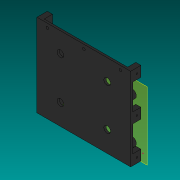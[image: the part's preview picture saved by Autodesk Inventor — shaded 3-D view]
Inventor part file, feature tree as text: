
AUTODESK INVENTOR PART (.ipt)
format: ipt  version: 2019 (Build 230136000, 136)  size: 277,504 bytes
history: native  units: mm
features: sketch x17, extrude x14, reference x8, fillet x3, other x2, plane x1
ambient origin geometry x8: Origin, YZ Plane, XZ Plane, XY Plane, X Axis, Y Axis, Z Axis, Center Point
bodies: Solid1 (feature_tree)
feature tree (45):
  plane  "Work Plane1"
  extrude  "Extrusion1"  Depth=8.0mm
  extrude  "Extrusion2"  Depth=8.0mm
  extrude  "Extrusion3"  Depth=10.0mm
  extrude  "Extrusion4"  Depth=1.5mm
  sketch  "Sketch5"  dims[d9=1.5mm d10=10.0mm d11=0.0mm]
  sketch  "Sketch6"  dims[d16=2.0mm d17=0.0mm d18=6.5mm d19=6.5mm]
  extrude  "Extrusion5"  Depth=10.0mm TaperAngle=0.0deg
  extrude  "Extrusion6"  Depth=2.0mm
  fillet  "Fillet1"  Radius=6.5mm
  extrude  "Extrusion7"  Depth=6.5mm
  extrude  "Extrusion8"  Depth=8.0mm
  fillet  "Fillet2"  Radius=10.0mm
  extrude  "Extrusion9"  Depth=5.0mm TaperAngle=0.0deg
  sketch  "Sketch12"  dims[d35=10.0mm d36=8.0mm]
  fillet  "Fillet3"  Radius=10.0mm
  extrude  "Extrusion10"  Depth=8.0mm
  extrude  "Extrusion11"  Depth=1.0mm
  extrude  "Extrusion12"  Depth=8.0mm
  extrude  "Extrusion13"  Depth=5.0mm TaperAngle=0.0deg
  extrude  "Extrusion14"  Depth=10.0mm
  sketch  "Sketch1"  dims[d0=8.0mm d1=8.0mm]
  reference  "Reference1"
  reference  "Reference2"
  reference  "Reference3"
  reference  "Reference4"
  sketch  "Sketch2"  dims[d2=8.0mm d3=8.0mm]
  sketch  "Sketch3"  dims[d4=10.0mm d5=0.0mm d6=1.5mm]
  reference  "Reference5"
  reference  "Reference6"
  reference  "Reference7"
  reference  "Reference8"
  sketch  "Sketch4"  dims[d7=1.5mm d8=1.5mm]
  sketch  "Sketch7"  dims[d20=6.5mm d21=6.5mm]
  sketch  "Sketch8"  dims[d22=2.0mm d23=0.0mm d24=8.0mm d25=10.0mm]
  sketch  "Sketch9"  dims[d26=1.5mm d27=5.0mm d28=0.0mm d29=10.0mm]
  sketch  "Sketch10"  dims[d30=8.0mm d31=1.5mm]
  sketch  "Sketch11"  dims[d32=5.0mm d33=0.0mm d34=1.0mm]
  sketch  "Sketch13"  dims[d37=1.5mm d38=5.0mm d39=0.0mm]
  sketch  "Sketch14"  dims[d40=8.0mm d41=10.0mm]
  sketch  "Sketch15"  dims[d42=1.5mm]
  sketch  "Sketch16"  dims[d43=5.0mm d44=0.0mm]
  sketch  "Sketch17"  dims[d45=1.0mm d47=1.5mm d48=5.0mm d49=8.0mm d50=10.0mm d51=5.0mm d52=0.0mm d53=1.0mm d56=1.5mm d57=5.0mm d58=8.0mm d59=10.0mm d60=8.0mm d61=5.0mm d62=0.0mm d63=1.5mm d65=8.0mm d66=10.0mm d67=8.0mm d68=5.0mm d69=0.0mm d70=8.0mm d71=10.0mm d73=1.5mm d74=5.0mm d75=0.0mm d76=5.0mm d77=0.0mm d79=2.5mm d83=2.5mm d85=2.5mm d86=2.0mm d87=0.0mm]
  other  "Ensamblaje Reloj LCD 16x2.iam"
  other  "PCB Down:1"
